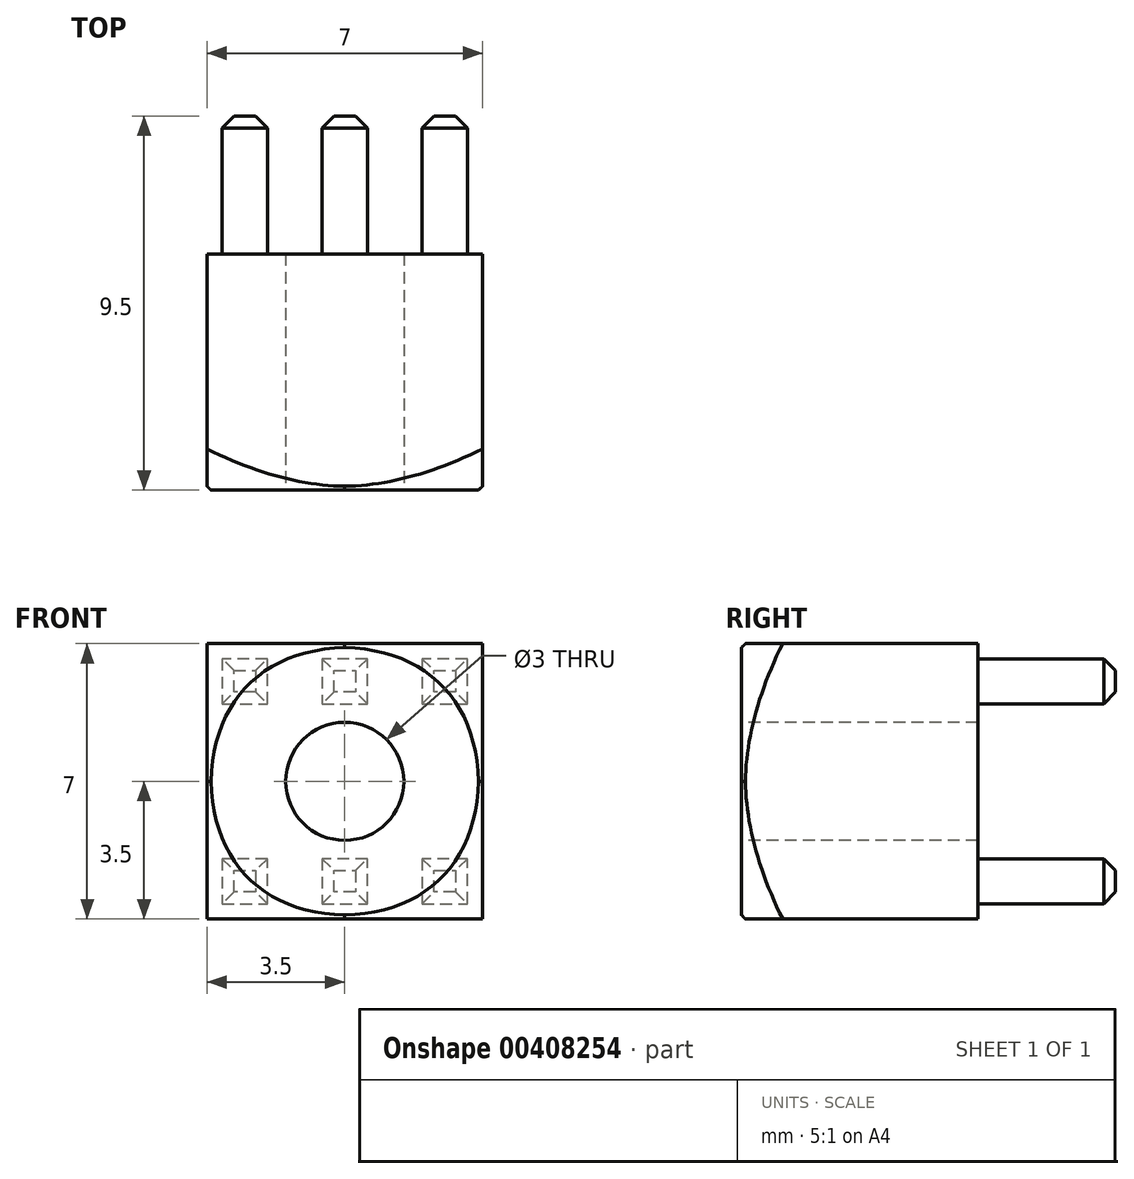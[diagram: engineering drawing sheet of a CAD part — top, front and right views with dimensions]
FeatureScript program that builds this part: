
annotation { "Feature Type Name" : "Feature", "Feature Type Description" : "" }
export const myFeature = defineFeature(function(context is Context, id is Id, definition is map)
    precondition{}
    {
        {
            var Q0;
            Q0=qCreatedBy(makeId("Front.planeOp"),FACE);
            var sketch = newSketch(context, id + "F0", { "sketchPlane" : qUnion([Q0])});
            skLineSegment(sketch, "E0.bottom", {"start": v(-3.5, 3.5) * mm, "end": v(3.5, 3.5) * mm});
            skLineSegment(sketch, "E0.top", {"start": v(-3.5, -3.5) * mm, "end": v(3.5, -3.5) * mm});
            skLineSegment(sketch, "E0.left", {"start": v(-3.5, 3.5) * mm, "end": v(-3.5, -3.5) * mm});
            skLineSegment(sketch, "E0.right", {"start": v(3.5, 3.5) * mm, "end": v(3.5, -3.5) * mm});
            skPoint(sketch, "E0.middle", {"position": v(0, 0) * mm});
            skLineSegment(sketch, "E1", {"start": v(0, 3.5) * mm, "end": v(0, -3.5) * mm, "construction": true});
            skLineSegment(sketch, "E2", {"start": v(-3.5, 0) * mm, "end": v(3.5, 0) * mm, "construction": true});
            skLineSegment(sketch, "E3.bottom", {"start": v(1.97, 1.97) * mm, "end": v(3.12, 1.97) * mm});
            skLineSegment(sketch, "E3.top", {"start": v(1.97, 3.12) * mm, "end": v(3.12, 3.12) * mm});
            skLineSegment(sketch, "E3.left", {"start": v(1.97, 1.97) * mm, "end": v(1.97, 3.12) * mm});
            skLineSegment(sketch, "E3.right", {"start": v(3.12, 1.97) * mm, "end": v(3.12, 3.12) * mm});
            skPoint(sketch, "E3.middle", {"position": v(2.54, 2.54) * mm});
            skLineSegment(sketch, "E4.MirrorCS", {"start": v(-1.97, 3.11) * mm, "end": v(-3.12, 3.11) * mm});
            skLineSegment(sketch, "E5.MirrorCS", {"start": v(-1.97, 1.96) * mm, "end": v(-1.97, 3.11) * mm});
            skLineSegment(sketch, "E6.MirrorCS", {"start": v(-1.97, 1.96) * mm, "end": v(-3.12, 1.96) * mm});
            skLineSegment(sketch, "E7.MirrorCS", {"start": v(-3.12, 1.96) * mm, "end": v(-3.12, 3.11) * mm});
            skPoint(sketch, "E8.MirrorP", {"position": v(-2.54, 2.54) * mm});
            skLineSegment(sketch, "E9.MirrorCS", {"start": v(1.97, -1.96) * mm, "end": v(3.12, -1.96) * mm});
            skLineSegment(sketch, "E10.MirrorCS", {"start": v(1.97, -1.96) * mm, "end": v(1.97, -3.11) * mm});
            skLineSegment(sketch, "E11.MirrorCS", {"start": v(1.97, -3.11) * mm, "end": v(3.12, -3.11) * mm});
            skLineSegment(sketch, "E12.MirrorCS", {"start": v(3.12, -1.96) * mm, "end": v(3.12, -3.11) * mm});
            skPoint(sketch, "E13.MirrorP", {"position": v(2.54, -2.54) * mm});
            skLineSegment(sketch, "E14.MirrorCS", {"start": v(-1.97, -1.97) * mm, "end": v(-3.12, -1.97) * mm});
            skLineSegment(sketch, "E15.MirrorCS", {"start": v(-3.12, -1.97) * mm, "end": v(-3.12, -3.12) * mm});
            skLineSegment(sketch, "E16.MirrorCS", {"start": v(-1.97, -3.12) * mm, "end": v(-3.12, -3.12) * mm});
            skLineSegment(sketch, "E17.MirrorCS", {"start": v(-1.97, -1.96) * mm, "end": v(-1.97, -3.11) * mm});
            skPoint(sketch, "E18.MirrorP", {"position": v(-2.54, -2.54) * mm});
            skLineSegment(sketch, "E19.bottom", {"start": v(-0.57, -3.12) * mm, "end": v(0.58, -3.12) * mm});
            skLineSegment(sketch, "E19.top", {"start": v(-0.57, -1.97) * mm, "end": v(0.58, -1.97) * mm});
            skLineSegment(sketch, "E19.left", {"start": v(-0.57, -3.12) * mm, "end": v(-0.57, -1.97) * mm});
            skLineSegment(sketch, "E19.right", {"start": v(0.58, -3.12) * mm, "end": v(0.58, -1.97) * mm});
            skPoint(sketch, "E19.middle", {"position": v(0, -2.54) * mm});
            skLineSegment(sketch, "E20.MirrorCS", {"start": v(-0.58, 1.97) * mm, "end": v(0.57, 1.97) * mm});
            skLineSegment(sketch, "E21.MirrorCS", {"start": v(0.57, 3.12) * mm, "end": v(0.57, 1.97) * mm});
            skLineSegment(sketch, "E22.MirrorCS", {"start": v(-0.58, 3.11) * mm, "end": v(0.57, 3.12) * mm});
            skPoint(sketch, "E23.MirrorP", {"position": v(0, 2.54) * mm});
            skLineSegment(sketch, "E24.MirrorCS", {"start": v(-0.58, 3.11) * mm, "end": v(-0.58, 1.97) * mm});
            skSolve(sketch);
        }
        {
            var Q0;
            Q0=makeQuery(id+"F0.imprint","IMPRINT",FACE,{"disambiguationData":[TD([[makeQuery(id+"F0.imprint","IMPRINT",EDGE,{"derivedFrom":sQuery(id+"F0.wireOp",EDGE,"E0.bottom")}),-1.0]])]});
            var Q1;
            Q1=makeQuery(id+"F0.imprint","IMPRINT",FACE,{"disambiguationData":[TD([[makeQuery(id+"F0.imprint","IMPRINT",EDGE,{"derivedFrom":sQuery(id+"F0.wireOp",EDGE,"E14.MirrorCS")}),1.0]])]});
            var Q2;
            Q2=makeQuery(id+"F0.imprint","IMPRINT",FACE,{"disambiguationData":[TD([[makeQuery(id+"F0.imprint","IMPRINT",EDGE,{"derivedFrom":sQuery(id+"F0.wireOp",EDGE,"E19.bottom")}),1.0]])]});
            var Q3;
            Q3=makeQuery(id+"F0.imprint","IMPRINT",FACE,{"disambiguationData":[TD([[makeQuery(id+"F0.imprint","IMPRINT",EDGE,{"derivedFrom":sQuery(id+"F0.wireOp",EDGE,"E20.MirrorCS")}),1.0]])]});
            var Q4;
            Q4=makeQuery(id+"F0.imprint","IMPRINT",FACE,{"disambiguationData":[TD([[makeQuery(id+"F0.imprint","IMPRINT",EDGE,{"derivedFrom":sQuery(id+"F0.wireOp",EDGE,"E4.MirrorCS")}),1.0]])]});
            var Q5;
            Q5=makeQuery(id+"F0.imprint","IMPRINT",FACE,{"disambiguationData":[TD([[makeQuery(id+"F0.imprint","IMPRINT",EDGE,{"derivedFrom":sQuery(id+"F0.wireOp",EDGE,"E3.bottom")}),1.0]])]});
            var Q6;
            Q6=makeQuery(id+"F0.imprint","IMPRINT",FACE,{"disambiguationData":[TD([[makeQuery(id+"F0.imprint","IMPRINT",EDGE,{"derivedFrom":sQuery(id+"F0.wireOp",EDGE,"E9.MirrorCS")}),-1.0]])]});
            extrude(context, id + "F1", {"entities" : qUnion([Q0, Q1, Q2, Q3, Q4, Q5, Q6]), "depth" : 6 * mm});
        }
        {
            var Q0;
            Q0=makeQuery(id+"F1.opExtrude","CAP_EDGE",EDGE,{"disambiguationData":[OSD([sQuery(id+"F0.wireOp",EDGE,"E0.right")])],"isStart":false});
            var Q1;
            Q1=makeQuery(id+"F1.opExtrude","CAP_EDGE",EDGE,{"disambiguationData":[OSD([sQuery(id+"F0.wireOp",EDGE,"E0.bottom")])],"isStart":false});
            var Q2;
            Q2=makeQuery(id+"F1.opExtrude","CAP_EDGE",EDGE,{"disambiguationData":[OSD([sQuery(id+"F0.wireOp",EDGE,"E0.left")])],"isStart":false});
            var Q3;
            Q3=makeQuery(id+"F1.opExtrude","CAP_EDGE",EDGE,{"disambiguationData":[OSD([sQuery(id+"F0.wireOp",EDGE,"E0.top")])],"isStart":false});
            chamfer(context, id + "F2", {"entities" : qUnion([Q0, Q1, Q2, Q3]), "width" : 0.1 * mm, "tangentPropagation" : true});
        }
        {
            var Q0;
            Q0=makeQuery(id+"F2.opChamfer","BLEND_EDGE",EDGE,{"blendedFrom":[makeQuery(id+"F1.opExtrude","CAP_EDGE",EDGE,{"disambiguationData":[OSD([sQuery(id+"F0.wireOp",EDGE,"E0.bottom")])],"isStart":false}),makeQuery(id+"F1.opExtrude","CAP_EDGE",EDGE,{"disambiguationData":[OSD([sQuery(id+"F0.wireOp",EDGE,"E0.right")])],"isStart":false})],"blendedInto":[]});
            var Q1;
            Q1=makeQuery(id+"F2.opChamfer","BLEND_EDGE",EDGE,{"blendedFrom":[makeQuery(id+"F1.opExtrude","CAP_EDGE",EDGE,{"disambiguationData":[OSD([sQuery(id+"F0.wireOp",EDGE,"E0.bottom")])],"isStart":false}),makeQuery(id+"F1.opExtrude","CAP_EDGE",EDGE,{"disambiguationData":[OSD([sQuery(id+"F0.wireOp",EDGE,"E0.left")])],"isStart":false})],"blendedInto":[]});
            var Q2;
            Q2=makeQuery(id+"F2.opChamfer","BLEND_EDGE",EDGE,{"blendedFrom":[makeQuery(id+"F1.opExtrude","CAP_EDGE",EDGE,{"disambiguationData":[OSD([sQuery(id+"F0.wireOp",EDGE,"E0.top")])],"isStart":false}),makeQuery(id+"F1.opExtrude","CAP_EDGE",EDGE,{"disambiguationData":[OSD([sQuery(id+"F0.wireOp",EDGE,"E0.right")])],"isStart":false})],"blendedInto":[]});
            var Q3;
            Q3=makeQuery(id+"F2.opChamfer","BLEND_EDGE",EDGE,{"blendedFrom":[makeQuery(id+"F1.opExtrude","CAP_EDGE",EDGE,{"disambiguationData":[OSD([sQuery(id+"F0.wireOp",EDGE,"E0.top")])],"isStart":false}),makeQuery(id+"F1.opExtrude","CAP_EDGE",EDGE,{"disambiguationData":[OSD([sQuery(id+"F0.wireOp",EDGE,"E0.left")])],"isStart":false})],"blendedInto":[]});
            fillet(context, id + "F3", {"entities" : qUnion([Q0, Q1, Q2, Q3]), "radius" : 5 * mm, "tangentPropagation" : true, "allowEdgeOverflow" : false});
        }
        {
            var Q0;
            Q0=makeQuery(id+"F1.opExtrude","CAP_FACE",FACE,{"disambiguationData":[OSD([sQuery(id+"F0.wireOp",EDGE,"E0.bottom"),sQuery(id+"F0.wireOp",EDGE,"E0.top"),sQuery(id+"F0.wireOp",EDGE,"E0.left"),sQuery(id+"F0.wireOp",EDGE,"E0.right")])],"isStart":false});
            cPlane(context, id + "F4", {"entities" : qUnion([Q0]), "cplaneType" : CPlaneType.OFFSET, "offset" : 0 * mm, "width" : 150 * mm, "height" : 150 * mm});
        }
        {
            var Q0;
            Q0=qCreatedBy(id+"F4.planeOp",FACE);
            var sketch = newSketch(context, id + "F5", { "sketchPlane" : qUnion([Q0])});
            skPoint(sketch, "E25", {"position": v(0, 0) * mm});
            skSolve(sketch);
        }
        {
            var Q0;
            Q0=sQuery(id+"F5.wireOp",VERTEX,"E25");
            var Q1;
            Q1=makeQuery(id+"F1.opExtrude","SWEPT_BODY",BODY,{"disambiguationData":[OSD([sQuery(id+"F0.wireOp",EDGE,"E0.bottom"),sQuery(id+"F0.wireOp",EDGE,"E0.top"),sQuery(id+"F0.wireOp",EDGE,"E0.left"),sQuery(id+"F0.wireOp",EDGE,"E0.right")])]});
            hole(context, id + "F6", {"style" : HoleStyle.SIMPLE, "endStyle" : HoleEndStyle.BLIND, "holeDiameter" : 3 * mm, "holeDepth" : 6 * mm, "tappedDepth" : 12 * mm, "tapClearance" : 3, "locations" : qUnion([Q0]), "scope" : qUnion([Q1])});
        }
        {
            var Q0;
            Q0=makeQuery(id+"F1.opExtrude","CAP_FACE",FACE,{"disambiguationData":[OSD([sQuery(id+"F0.wireOp",EDGE,"E0.bottom"),sQuery(id+"F0.wireOp",EDGE,"E0.top"),sQuery(id+"F0.wireOp",EDGE,"E0.left"),sQuery(id+"F0.wireOp",EDGE,"E0.right")])],"isStart":true});
            cPlane(context, id + "F7", {"entities" : qUnion([Q0]), "cplaneType" : CPlaneType.OFFSET, "offset" : 0 * mm, "width" : 150 * mm, "height" : 150 * mm});
        }
        {
            var Q0;
            Q0=makeQuery(id+"F0.imprint","IMPRINT",FACE,{"disambiguationData":[TD([[makeQuery(id+"F0.imprint","IMPRINT",EDGE,{"derivedFrom":sQuery(id+"F0.wireOp",EDGE,"E3.bottom")}),1.0]])]});
            var Q1;
            Q1=makeQuery(id+"F0.imprint","IMPRINT",FACE,{"disambiguationData":[TD([[makeQuery(id+"F0.imprint","IMPRINT",EDGE,{"derivedFrom":sQuery(id+"F0.wireOp",EDGE,"E20.MirrorCS")}),1.0]])]});
            var Q2;
            Q2=makeQuery(id+"F0.imprint","IMPRINT",FACE,{"disambiguationData":[TD([[makeQuery(id+"F0.imprint","IMPRINT",EDGE,{"derivedFrom":sQuery(id+"F0.wireOp",EDGE,"E4.MirrorCS")}),1.0]])]});
            var Q3;
            Q3=makeQuery(id+"F0.imprint","IMPRINT",FACE,{"disambiguationData":[TD([[makeQuery(id+"F0.imprint","IMPRINT",EDGE,{"derivedFrom":sQuery(id+"F0.wireOp",EDGE,"E14.MirrorCS")}),1.0]])]});
            var Q4;
            Q4=makeQuery(id+"F0.imprint","IMPRINT",FACE,{"disambiguationData":[TD([[makeQuery(id+"F0.imprint","IMPRINT",EDGE,{"derivedFrom":sQuery(id+"F0.wireOp",EDGE,"E19.bottom")}),1.0]])]});
            var Q5;
            Q5=makeQuery(id+"F0.imprint","IMPRINT",FACE,{"disambiguationData":[TD([[makeQuery(id+"F0.imprint","IMPRINT",EDGE,{"derivedFrom":sQuery(id+"F0.wireOp",EDGE,"E9.MirrorCS")}),-1.0]])]});
            extrude(context, id + "F8", {"entities" : qUnion([Q0, Q1, Q2, Q3, Q4, Q5]), "oppositeDirection" : true, "depth" : 3.5 * mm});
        }
        {
            var Q0;
            Q0=makeQuery(id+"F8.opExtrude","CAP_EDGE",EDGE,{"disambiguationData":[OSD([sQuery(id+"F0.wireOp",EDGE,"E11.MirrorCS")])],"isStart":false});
            var Q1;
            Q1=makeQuery(id+"F8.opExtrude","CAP_EDGE",EDGE,{"disambiguationData":[OSD([sQuery(id+"F0.wireOp",EDGE,"E10.MirrorCS")])],"isStart":false});
            var Q2;
            Q2=makeQuery(id+"F8.opExtrude","CAP_EDGE",EDGE,{"disambiguationData":[OSD([sQuery(id+"F0.wireOp",EDGE,"E12.MirrorCS")])],"isStart":false});
            var Q3;
            Q3=makeQuery(id+"F8.opExtrude","CAP_EDGE",EDGE,{"disambiguationData":[OSD([sQuery(id+"F0.wireOp",EDGE,"E9.MirrorCS")])],"isStart":false});
            var Q4;
            Q4=makeQuery(id+"F8.opExtrude","CAP_EDGE",EDGE,{"disambiguationData":[OSD([sQuery(id+"F0.wireOp",EDGE,"E19.right")])],"isStart":false});
            var Q5;
            Q5=makeQuery(id+"F8.opExtrude","CAP_EDGE",EDGE,{"disambiguationData":[OSD([sQuery(id+"F0.wireOp",EDGE,"E19.bottom")])],"isStart":false});
            var Q6;
            Q6=makeQuery(id+"F8.opExtrude","CAP_EDGE",EDGE,{"disambiguationData":[OSD([sQuery(id+"F0.wireOp",EDGE,"E19.left")])],"isStart":false});
            var Q7;
            Q7=makeQuery(id+"F8.opExtrude","CAP_EDGE",EDGE,{"disambiguationData":[OSD([sQuery(id+"F0.wireOp",EDGE,"E19.top")])],"isStart":false});
            var Q8;
            Q8=makeQuery(id+"F8.opExtrude","CAP_EDGE",EDGE,{"disambiguationData":[OSD([sQuery(id+"F0.wireOp",EDGE,"E17.MirrorCS")])],"isStart":false});
            var Q9;
            Q9=makeQuery(id+"F8.opExtrude","CAP_EDGE",EDGE,{"disambiguationData":[OSD([sQuery(id+"F0.wireOp",EDGE,"E14.MirrorCS")])],"isStart":false});
            var Q10;
            Q10=makeQuery(id+"F8.opExtrude","CAP_EDGE",EDGE,{"disambiguationData":[OSD([sQuery(id+"F0.wireOp",EDGE,"E15.MirrorCS")])],"isStart":false});
            var Q11;
            Q11=makeQuery(id+"F8.opExtrude","CAP_EDGE",EDGE,{"disambiguationData":[OSD([sQuery(id+"F0.wireOp",EDGE,"E16.MirrorCS")])],"isStart":false});
            var Q12;
            Q12=makeQuery(id+"F8.opExtrude","CAP_EDGE",EDGE,{"disambiguationData":[OSD([sQuery(id+"F0.wireOp",EDGE,"E3.right")])],"isStart":false});
            var Q13;
            Q13=makeQuery(id+"F8.opExtrude","CAP_EDGE",EDGE,{"disambiguationData":[OSD([sQuery(id+"F0.wireOp",EDGE,"E3.bottom")])],"isStart":false});
            var Q14;
            Q14=makeQuery(id+"F8.opExtrude","CAP_EDGE",EDGE,{"disambiguationData":[OSD([sQuery(id+"F0.wireOp",EDGE,"E3.left")])],"isStart":false});
            var Q15;
            Q15=makeQuery(id+"F8.opExtrude","CAP_EDGE",EDGE,{"disambiguationData":[OSD([sQuery(id+"F0.wireOp",EDGE,"E3.top")])],"isStart":false});
            var Q16;
            Q16=makeQuery(id+"F8.opExtrude","CAP_EDGE",EDGE,{"disambiguationData":[OSD([sQuery(id+"F0.wireOp",EDGE,"E21.MirrorCS")])],"isStart":false});
            var Q17;
            Q17=makeQuery(id+"F8.opExtrude","CAP_EDGE",EDGE,{"disambiguationData":[OSD([sQuery(id+"F0.wireOp",EDGE,"E22.MirrorCS")])],"isStart":false});
            var Q18;
            Q18=makeQuery(id+"F8.opExtrude","CAP_EDGE",EDGE,{"disambiguationData":[OSD([sQuery(id+"F0.wireOp",EDGE,"E24.MirrorCS")])],"isStart":false});
            var Q19;
            Q19=makeQuery(id+"F8.opExtrude","CAP_EDGE",EDGE,{"disambiguationData":[OSD([sQuery(id+"F0.wireOp",EDGE,"E20.MirrorCS")])],"isStart":false});
            var Q20;
            Q20=makeQuery(id+"F8.opExtrude","CAP_EDGE",EDGE,{"disambiguationData":[OSD([sQuery(id+"F0.wireOp",EDGE,"E5.MirrorCS")])],"isStart":false});
            var Q21;
            Q21=makeQuery(id+"F8.opExtrude","CAP_EDGE",EDGE,{"disambiguationData":[OSD([sQuery(id+"F0.wireOp",EDGE,"E6.MirrorCS")])],"isStart":false});
            var Q22;
            Q22=makeQuery(id+"F8.opExtrude","CAP_EDGE",EDGE,{"disambiguationData":[OSD([sQuery(id+"F0.wireOp",EDGE,"E7.MirrorCS")])],"isStart":false});
            var Q23;
            Q23=makeQuery(id+"F8.opExtrude","CAP_EDGE",EDGE,{"disambiguationData":[OSD([sQuery(id+"F0.wireOp",EDGE,"E4.MirrorCS")])],"isStart":false});
            chamfer(context, id + "F9", {"entities" : qUnion([Q0, Q1, Q2, Q3, Q4, Q5, Q6, Q7, Q8, Q9, Q10, Q11, Q12, Q13, Q14, Q15, Q16, Q17, Q18, Q19, Q20, Q21, Q22, Q23]), "width" : 0.3 * mm, "tangentPropagation" : true});
        }
    });
